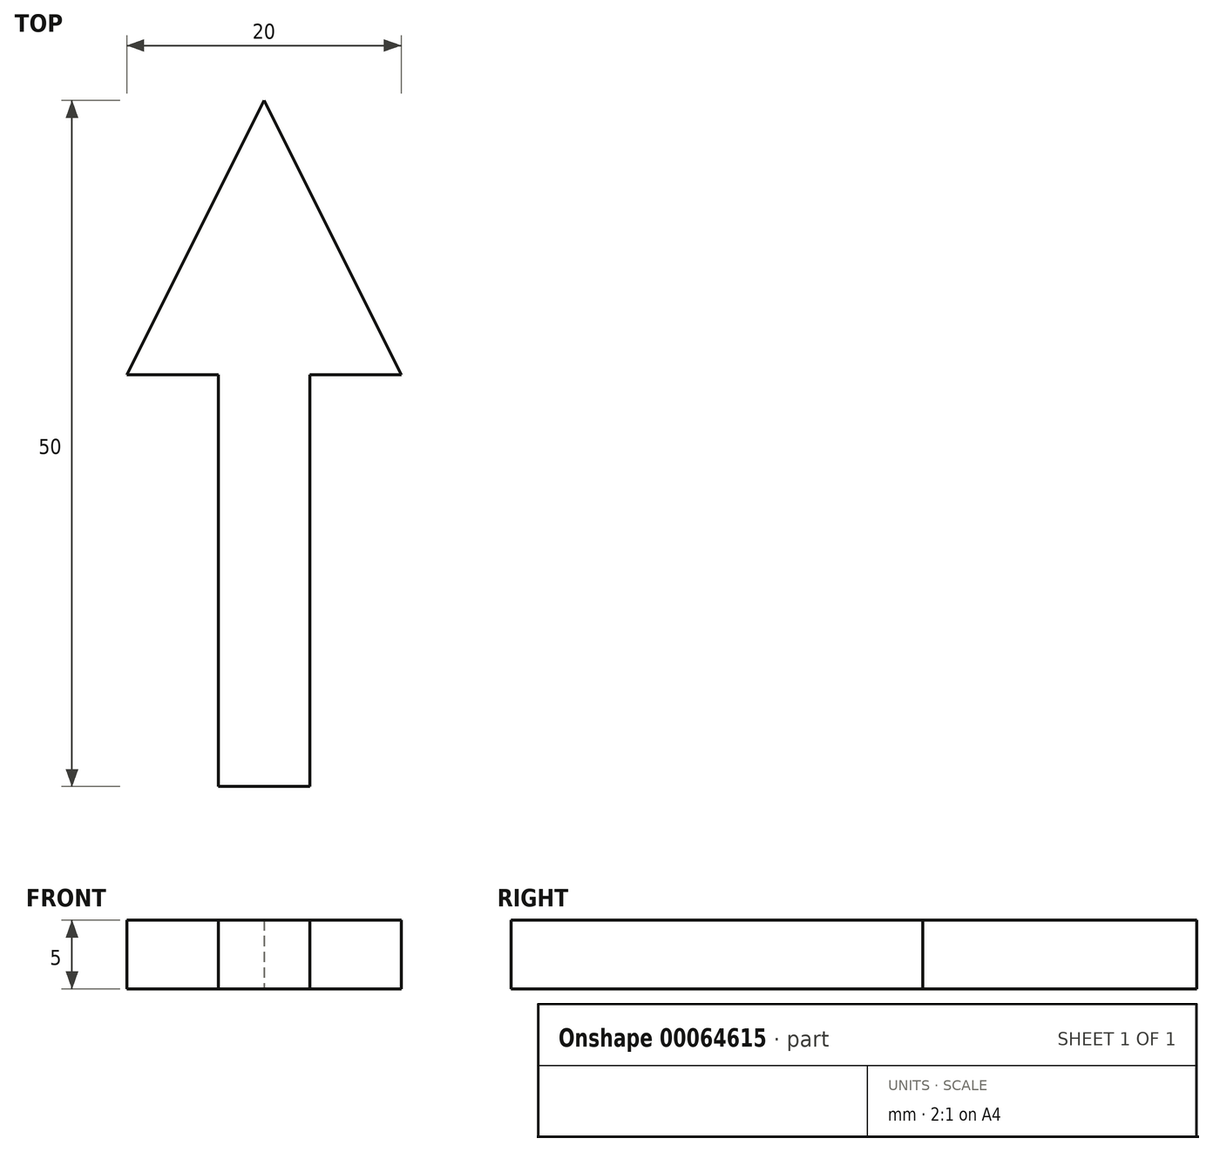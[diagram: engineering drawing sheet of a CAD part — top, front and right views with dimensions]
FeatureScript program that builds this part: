
annotation { "Feature Type Name" : "Feature", "Feature Type Description" : "" }
export const myFeature = defineFeature(function(context is Context, id is Id, definition is map)
    precondition{}
    {
        {
            var Q0;
            Q0=qCreatedBy(makeId("Top.planeOp"),FACE);
            var sketch = newSketch(context, id + "F0", { "sketchPlane" : qUnion([Q0])});
            skLineSegment(sketch, "E0", {"start": v(-3.33, -20) * mm, "end": v(-3.33, -50) * mm});
            skLineSegment(sketch, "E1", {"start": v(-3.33, -50) * mm, "end": v(3.33, -50) * mm});
            skLineSegment(sketch, "E2", {"start": v(3.33, -50) * mm, "end": v(3.33, -20) * mm});
            skLineSegment(sketch, "E3", {"start": v(3.33, -20) * mm, "end": v(10, -20) * mm});
            skLineSegment(sketch, "E4", {"start": v(10, -20) * mm, "end": v(0, 0) * mm});
            skLineSegment(sketch, "E5", {"start": v(0, 0) * mm, "end": v(-10, -20) * mm});
            skLineSegment(sketch, "E6", {"start": v(-10, -20) * mm, "end": v(-3.33, -20) * mm});
            skSolve(sketch);
        }
        {
            var Q0;
            Q0=makeQuery(id+"F0.imprint","IMPRINT",FACE,{"disambiguationData":[TD([[makeQuery(id+"F0.imprint","IMPRINT",EDGE,{"derivedFrom":sQuery(id+"F0.wireOp",EDGE,"E0")}),1.0]])]});
            extrude(context, id + "F1", {"entities" : qUnion([Q0]), "depth" : 5 * mm});
        }
    });
